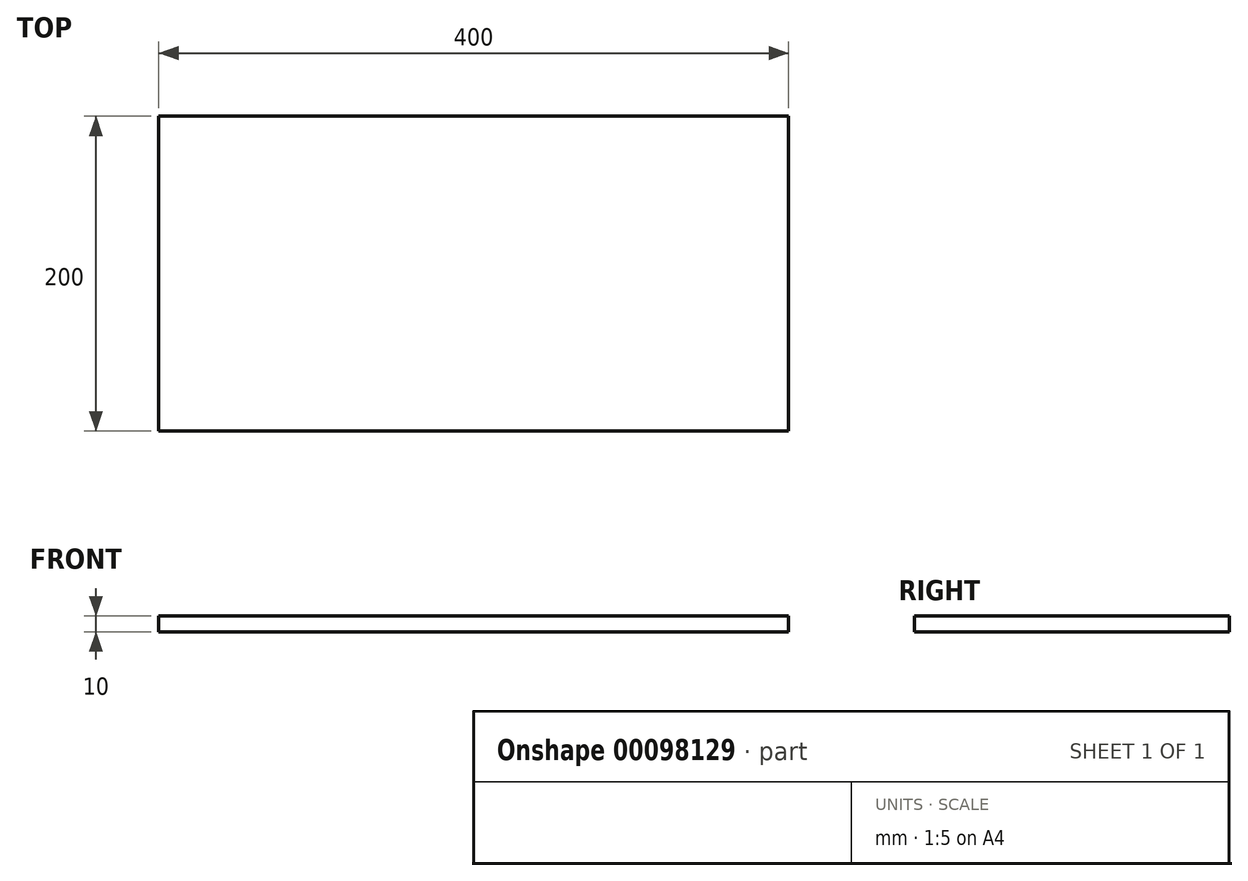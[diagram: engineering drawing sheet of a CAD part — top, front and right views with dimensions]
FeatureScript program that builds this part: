
annotation { "Feature Type Name" : "Feature", "Feature Type Description" : "" }
export const myFeature = defineFeature(function(context is Context, id is Id, definition is map)
    precondition{}
    {
        {
            var Q0;
            Q0=qCreatedBy(makeId("Top.planeOp"),FACE);
            var sketch = newSketch(context, id + "F0", { "sketchPlane" : qUnion([Q0])});
            skLineSegment(sketch, "E0.bottom", {"start": v(-200, 1238.24) * mm, "end": v(200, 1238.24) * mm});
            skLineSegment(sketch, "E0.top", {"start": v(-200, 1438.24) * mm, "end": v(200, 1438.24) * mm});
            skLineSegment(sketch, "E0.left", {"start": v(-200, 1238.24) * mm, "end": v(-200, 1438.24) * mm});
            skLineSegment(sketch, "E0.right", {"start": v(200, 1238.24) * mm, "end": v(200, 1438.24) * mm});
            skPoint(sketch, "E0.middle", {"position": v(0, 1338.24) * mm});
            skSolve(sketch);
        }
        {
            var Q0;
            Q0=makeQuery(id+"F0.imprint","IMPRINT",FACE,{"disambiguationData":[TD([[makeQuery(id+"F0.imprint","IMPRINT",EDGE,{"derivedFrom":sQuery(id+"F0.wireOp",EDGE,"E0.bottom")}),1.0]])]});
            extrude(context, id + "F1", {"entities" : qUnion([Q0]), "depth" : 10 * mm});
        }
        {
            var Q0;
            Q0=makeQuery(id+"F1.opExtrude","SWEPT_BODY",BODY,{"disambiguationData":[OSD([sQuery(id+"F0.wireOp",EDGE,"E0.bottom"),sQuery(id+"F0.wireOp",EDGE,"E0.top"),sQuery(id+"F0.wireOp",EDGE,"E0.left"),sQuery(id+"F0.wireOp",EDGE,"E0.right")])]});
            transform(context, id + "F2", {"entities" : qUnion([Q0]), "transformType" : TransformType.TRANSLATION_3D, "dx" : 0 * mm, "dy" : -1335.28 * mm, "dz" : 0 * mm, "makeCopy" : false});
        }
    });
